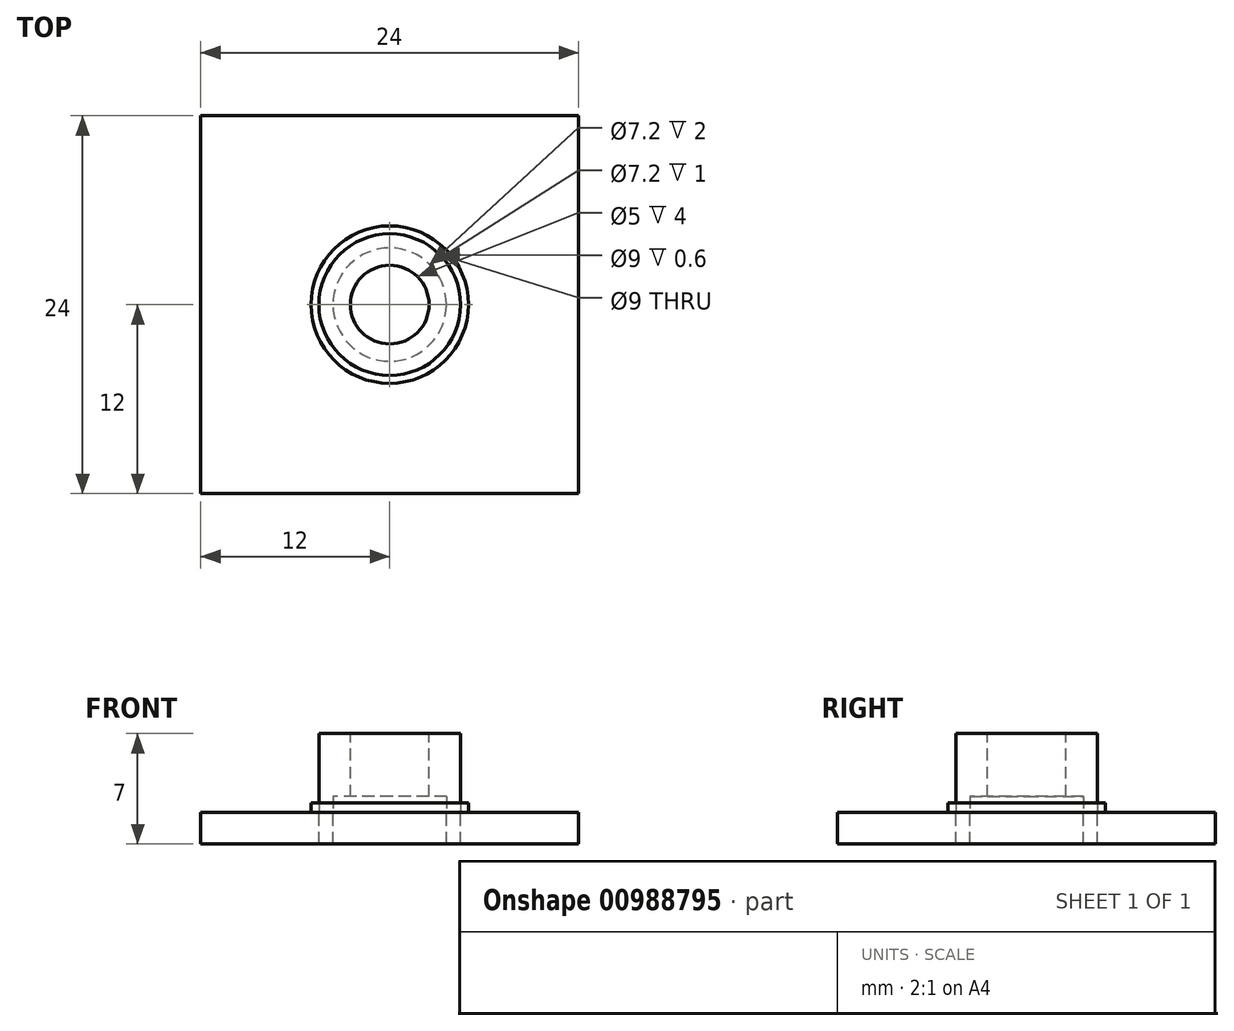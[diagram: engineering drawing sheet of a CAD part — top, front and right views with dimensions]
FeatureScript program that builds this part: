
annotation { "Feature Type Name" : "Feature", "Feature Type Description" : "" }
export const myFeature = defineFeature(function(context is Context, id is Id, definition is map)
    precondition{}
    {
        {
            var Q0;
            Q0=qCreatedBy(makeId("Top.planeOp"),FACE);
            var sketch = newSketch(context, id + "F0", { "sketchPlane" : qUnion([Q0])});
            skLineSegment(sketch, "E0.bottom", {"start": v(-12, 12) * mm, "end": v(12, 12) * mm});
            skLineSegment(sketch, "E0.top", {"start": v(-12, -12) * mm, "end": v(12, -12) * mm});
            skLineSegment(sketch, "E0.left", {"start": v(-12, 12) * mm, "end": v(-12, -12) * mm});
            skLineSegment(sketch, "E0.right", {"start": v(12, 12) * mm, "end": v(12, -12) * mm});
            skCircle(sketch, "E1", {"center": v(0, 0) * mm, "radius": 3.6 * mm});
            skCircle(sketch, "E2", {"center": v(0, 0) * mm, "radius": 4.5 * mm});
            skSolve(sketch);
        }
        {
            var Q0;
            Q0 = qSketchRegion(id + "F0", true);
            extrude(context, id + "F1", {"entities" : qUnion([Q0]), "depth" : -2 * mm, "offsetDistance" : 25 * mm});
        }
        {
            var Q0;
            Q0=makeQuery(id+"F0.imprint","IMPRINT",FACE,{"disambiguationData":[TD([[makeQuery(id+"F0.imprint","IMPRINT",EDGE,{"derivedFrom":sQuery(id+"F0.wireOp",EDGE,"E1")}),-1.0]])]});
            extrude(context, id + "F2", {"entities" : qUnion([Q0]), "depth" : 5 * mm, "offsetDistance" : 25 * mm});
        }
        {
            var Q0;
            Q0=makeQuery(id+"F2.opExtrude","CAP_FACE",FACE,{"disambiguationData":[OSD([sQuery(id+"F0.wireOp",EDGE,"E1"),sQuery(id+"F0.wireOp",EDGE,"E2")])],"isStart":false});
            var sketch = newSketch(context, id + "F3", { "sketchPlane" : qUnion([Q0])});
            skCircle(sketch, "E3", {"center": v(0, 0) * mm, "radius": 2.5 * mm});
            skSolve(sketch);
        }
        {
            var Q0;
            Q0=makeQuery(id+"F3.imprint","IMPRINT",FACE,{"disambiguationData":[TD([[makeQuery(id+"F3.imprint","IMPRINT",EDGE,{"derivedFrom":sQuery(id+"F3.wireOp",EDGE,"E3")}),-1.0]])]});
            extrude(context, id + "F4", {"entities" : qUnion([Q0]), "operationType" : NewBodyOperationType.ADD, "depth" : -4 * mm, "offsetDistance" : 25 * mm});
        }
        {
            var Q0;
            Q0=makeQuery(id+"F2.opExtrude","CAP_FACE",FACE,{"disambiguationData":[OSD([sQuery(id+"F0.wireOp",EDGE,"E1"),sQuery(id+"F0.wireOp",EDGE,"E2")])],"isStart":true});
            extrude(context, id + "F5", {"entities" : qUnion([Q0]), "depth" : 2 * mm, "offsetDistance" : 25 * mm});
        }
        {
            var Q0;
            Q0=makeQuery(id+"F1.opExtrude","CAP_FACE",FACE,{"disambiguationData":[OSD([sQuery(id+"F0.wireOp",EDGE,"E0.bottom"),sQuery(id+"F0.wireOp",EDGE,"E0.top"),sQuery(id+"F0.wireOp",EDGE,"E0.left"),sQuery(id+"F0.wireOp",EDGE,"E0.right"),sQuery(id+"F0.wireOp",EDGE,"E2")])],"isStart":true});
            var sketch = newSketch(context, id + "F6", { "sketchPlane" : qUnion([Q0])});
            skCircle(sketch, "E4", {"center": v(0, 0) * mm, "radius": 5 * mm});
            skSolve(sketch);
        }
        {
            var Q0;
            Q0=makeQuery(id+"F6.imprint","IMPRINT",FACE,{"disambiguationData":[TD([[makeQuery(id+"F6.imprint","IMPRINT",EDGE,{"derivedFrom":sQuery(id+"F6.wireOp",EDGE,"E4")}),1.0]])]});
            extrude(context, id + "F7", {"entities" : qUnion([Q0]), "depth" : 0.6 * mm, "offsetDistance" : 25 * mm});
        }
    });
